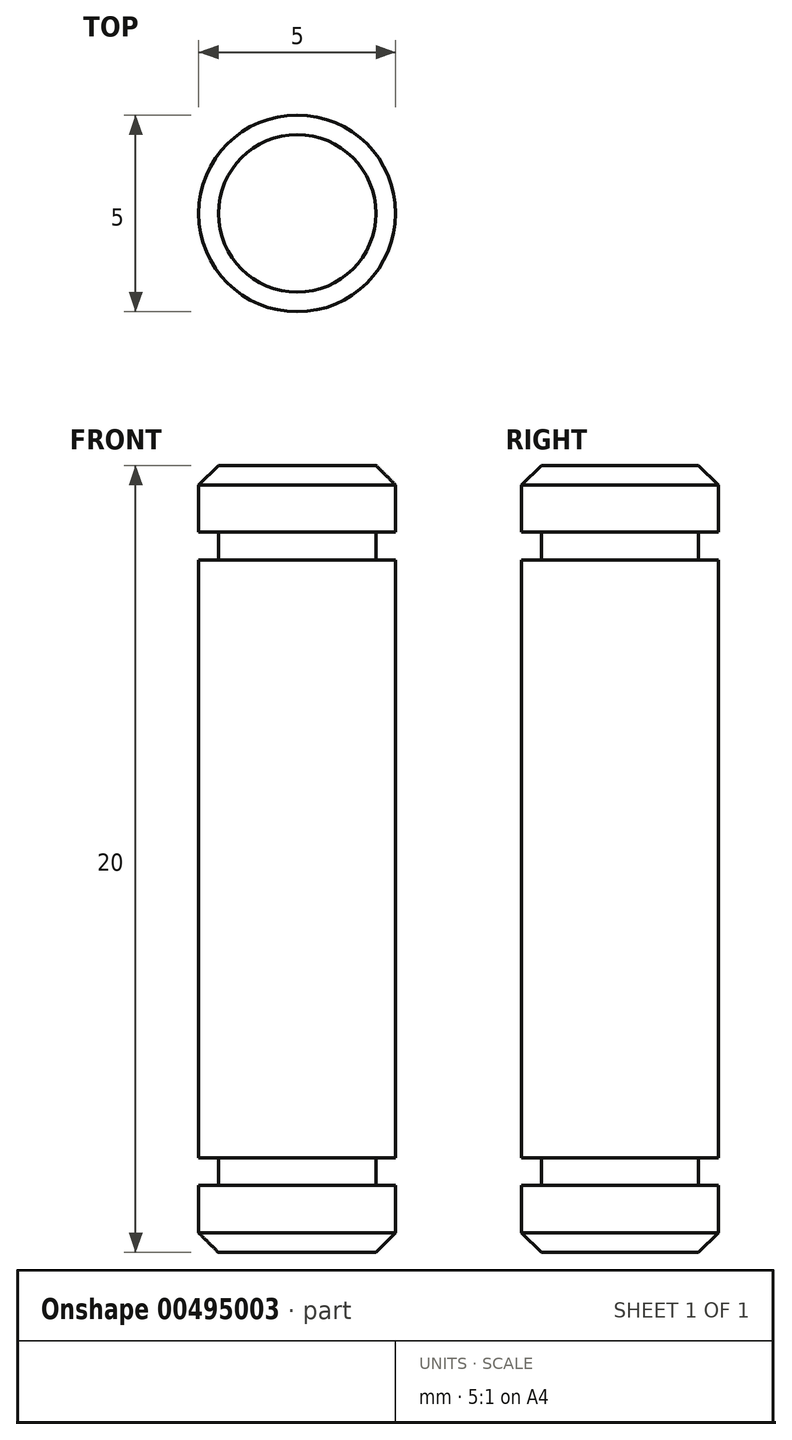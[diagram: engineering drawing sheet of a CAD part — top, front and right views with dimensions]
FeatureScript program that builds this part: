
annotation { "Feature Type Name" : "Feature", "Feature Type Description" : "" }
export const myFeature = defineFeature(function(context is Context, id is Id, definition is map)
    precondition{}
    {
        {
            var Q0;
            Q0=qCreatedBy(makeId("Top.planeOp"),FACE);
            cPlane(context, id + "F0", {"entities" : qUnion([Q0]), "cplaneType" : CPlaneType.OFFSET, "offset" : 7.6 * mm, "width" : 150 * mm, "height" : 150 * mm});
        }
        {
            var Q0;
            Q0=qCreatedBy(makeId("Top.planeOp"),FACE);
            var sketch = newSketch(context, id + "F1", { "sketchPlane" : qUnion([Q0])});
            skCircle(sketch, "E0", {"center": v(0, 0) * mm, "radius": 2.5 * mm});
            skSolve(sketch);
        }
        {
            var Q0;
            Q0=qSketchRegion(id+"F1",true);
            extrude(context, id + "F2", {"entities" : qUnion([Q0]), "depth" : 10 * mm});
        }
        {
            var Q0;
            Q0=qCreatedBy(id+"F0.planeOp",FACE);
            var sketch = newSketch(context, id + "F3", { "sketchPlane" : qUnion([Q0])});
            skCircle(sketch, "E1", {"center": v(0, 0) * mm, "radius": 2.5 * mm});
            skCircle(sketch, "E2", {"center": v(0, 0) * mm, "radius": 2 * mm});
            skSolve(sketch);
        }
        {
            var Q0;
            Q0=qSketchRegion(id+"F3",true);
            extrude(context, id + "F4", {"entities" : qUnion([Q0]), "operationType" : NewBodyOperationType.REMOVE, "depth" : .7 * mm});
        }
        {
            var Q0;
            Q0=makeQuery(id+"F2.opExtrude","SWEPT_BODY",BODY,{"disambiguationData":[OSD([sQuery(id+"F1.wireOp",EDGE,"E0")])]});
            var Q1;
            Q1=qCreatedBy(makeId("Top.planeOp"),FACE);
            mirror(context, id + "F5", {"operationType" : NewBodyOperationType.ADD, "entities" : qUnion([Q0]), "mirrorPlane" : qUnion([Q1])});
        }
        {
            var Q0;
            Q0=makeQuery(id+"F2.opExtrude","CAP_EDGE",EDGE,{"disambiguationData":[OSD([sQuery(id+"F1.wireOp",EDGE,"E0")])],"isStart":false});
            var Q1;
            Q1=makeQuery(id+"F5.opPattern","COPY",EDGE,{"derivedFrom":makeQuery(id+"F2.opExtrude","CAP_EDGE",EDGE,{"disambiguationData":[OSD([sQuery(id+"F1.wireOp",EDGE,"E0")])],"isStart":false}),"instanceName":"1"});
            chamfer(context, id + "F6", {"entities" : qUnion([Q0, Q1]), "width" : .5 * mm, "tangentPropagation" : true});
        }
    });
